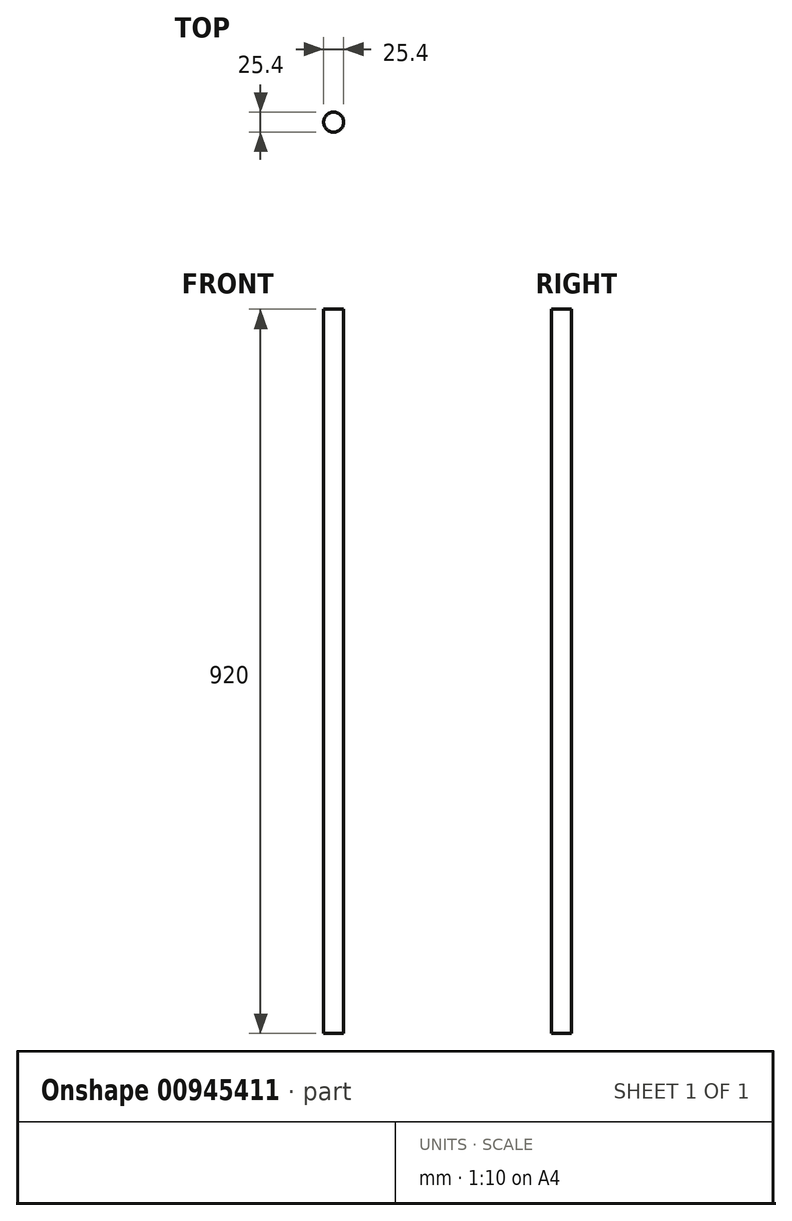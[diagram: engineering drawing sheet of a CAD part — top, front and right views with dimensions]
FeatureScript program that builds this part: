
annotation { "Feature Type Name" : "Feature", "Feature Type Description" : "" }
export const myFeature = defineFeature(function(context is Context, id is Id, definition is map)
    precondition{}
    {
        {
            var Q0;
            Q0=qCreatedBy(makeId("Top.planeOp"),FACE);
            var sketch = newSketch(context, id + "F0", { "sketchPlane" : qUnion([Q0])});
            skCircle(sketch, "E0", {"center": v(0, 0) * mm, "radius": 12.7 * mm});
            skSolve(sketch);
        }
        {
            var Q0;
            Q0=sQuery(id+"F0.wireOp",EDGE,"E0");
            extrude(context, id + "F1", {"bodyType" : ToolBodyType.SURFACE, "surfaceEntities" : qUnion([Q0]), "depth" : 920 * mm, "offsetDistance" : 25.4 * mm});
        }
    });
